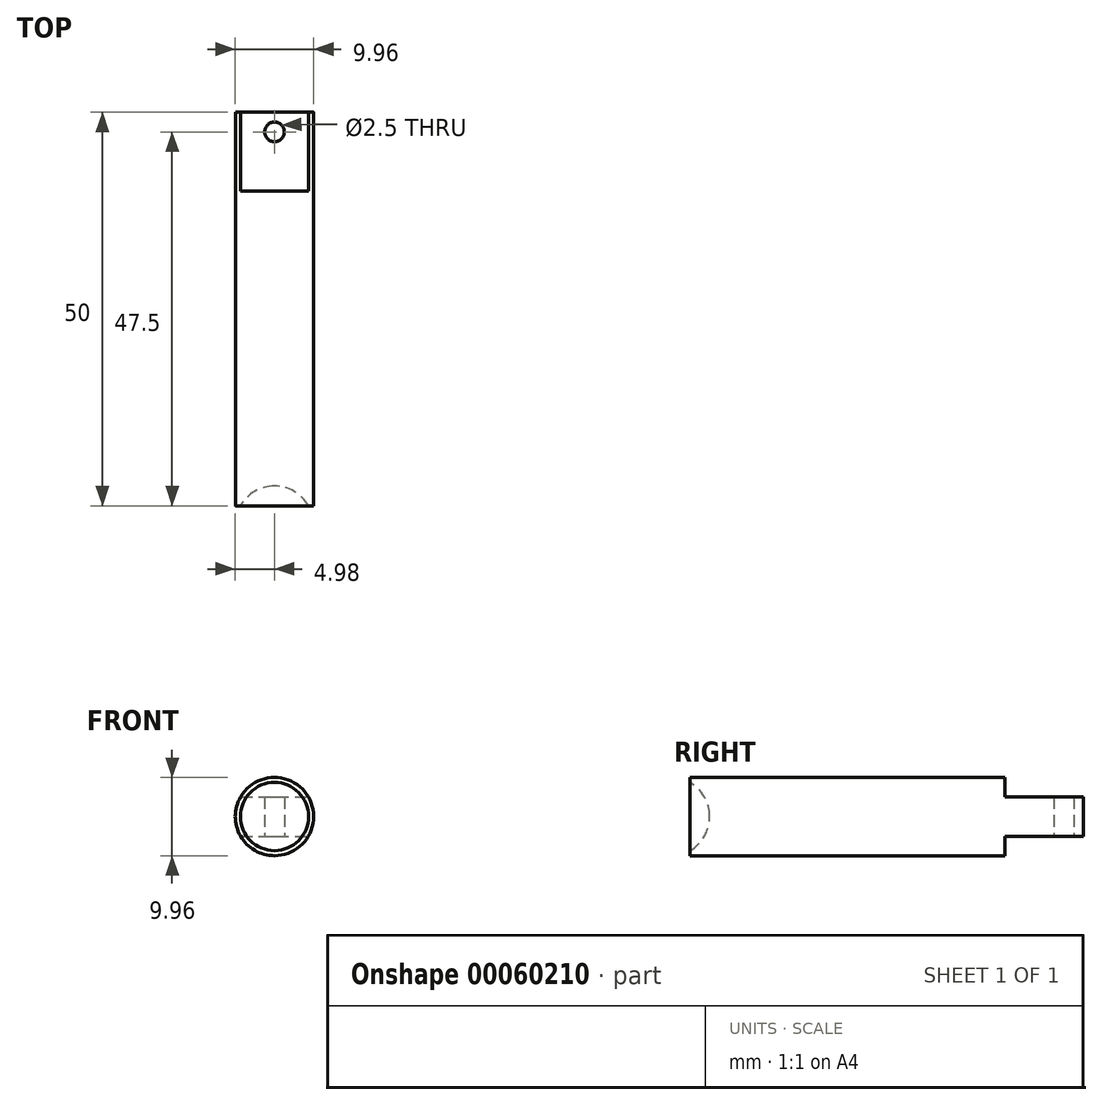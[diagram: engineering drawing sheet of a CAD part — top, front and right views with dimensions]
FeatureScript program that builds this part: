
annotation { "Feature Type Name" : "Feature", "Feature Type Description" : "" }
export const myFeature = defineFeature(function(context is Context, id is Id, definition is map)
    precondition{}
    {
        {
            var Q0;
            Q0=qCreatedBy(makeId("Front.planeOp"),FACE);
            var sketch = newSketch(context, id + "F0", { "sketchPlane" : qUnion([Q0])});
            skCircle(sketch, "E0", {"center": v(0, 0) * mm, "radius": 4.98 * mm});
            skSolve(sketch);
        }
        {
            var Q0;
            Q0 = qSketchRegion(id + "F0", true);
            extrude(context, id + "F1", {"entities" : qUnion([Q0]), "depth" : 50 * mm});
        }
        {
            var Q0;
            Q0=qCreatedBy(makeId("Right.planeOp"),FACE);
            var sketch = newSketch(context, id + "F2", { "sketchPlane" : qUnion([Q0])});
            skArc(sketch, "E1", {"start": v(-47.5, 0) * mm, "mid": v(-48.17, 2.5) * mm, "end": v(-50, 4.33) * mm});
            skLineSegment(sketch, "E2", {"start": v(-50, 4.33) * mm, "end": v(-52.5, 0) * mm});
            skLineSegment(sketch, "E3", {"start": v(-52.5, 0) * mm, "end": v(-47.5, 0) * mm});
            skPoint(sketch, "E4.orphan", {"position": v(-50, -4.33) * mm});
            skSolve(sketch);
        }
        {
            var Q0;
            Q0 = qSketchRegion(id + "F2", true);
            var Q1;
            Q1=sQuery(id+"F2.wireOp",EDGE,"E3");
            revolve(context, id + "F3", {"operationType" : NewBodyOperationType.REMOVE, "entities" : qUnion([Q0]), "axis" : qUnion([Q1]), "revolveType" : RevolveType.FULL, "oppositeDirection" : true});
        }
        {
            var Q0;
            Q0=qCreatedBy(makeId("Right.planeOp"),FACE);
            var sketch = newSketch(context, id + "F4", { "sketchPlane" : qUnion([Q0])});
            skLineSegment(sketch, "E5.bottom", {"start": v(-10, 33.44) * mm, "end": v(26.94, 33.44) * mm});
            skLineSegment(sketch, "E5.top", {"start": v(-10, 2.5) * mm, "end": v(26.94, 2.5) * mm});
            skLineSegment(sketch, "E5.left", {"start": v(-10, 33.44) * mm, "end": v(-10, 2.5) * mm});
            skLineSegment(sketch, "E5.right", {"start": v(26.94, 33.44) * mm, "end": v(26.94, 2.5) * mm});
            skLineSegment(sketch, "E6.bottom", {"start": v(-10, -2.5) * mm, "end": v(26.96, -2.5) * mm});
            skLineSegment(sketch, "E6.top", {"start": v(-10, -54.36) * mm, "end": v(26.96, -54.36) * mm});
            skLineSegment(sketch, "E6.left", {"start": v(-10, -2.5) * mm, "end": v(-10, -54.36) * mm});
            skLineSegment(sketch, "E6.right", {"start": v(26.96, -2.5) * mm, "end": v(26.96, -54.36) * mm});
            skSolve(sketch);
        }
        {
            var Q0;
            Q0 = qSketchRegion(id + "F4", true);
            extrude(context, id + "F5", {"entities" : qUnion([Q0]), "operationType" : NewBodyOperationType.REMOVE, "endBound" : BoundingType.THROUGH_ALL, "oppositeDirection" : true, "depth" : 25 * mm, "hasSecondDirection" : true, "secondDirectionBound" : SecondDirectionBoundingType.THROUGH_ALL, "secondDirectionOppositeDirection" : false, "secondDirectionDepth" : 25 * mm});
        }
        {
            var Q0;
            Q0=makeQuery(id+"F5.boolean.opBoolean","COPY",FACE,{"derivedFrom":makeQuery(id+"F5.opExtrude","SWEPT_FACE",FACE,{"disambiguationData":[OSD([sQuery(id+"F4.wireOp",EDGE,"E6.bottom")])]})});
            var sketch = newSketch(context, id + "F6", { "sketchPlane" : qUnion([Q0])});
            skCircle(sketch, "E7", {"center": v(0, 2.5) * mm, "radius": 1.25 * mm});
            skSolve(sketch);
        }
        {
            var Q0;
            Q0 = qSketchRegion(id + "F6", true);
            extrude(context, id + "F7", {"entities" : qUnion([Q0]), "operationType" : NewBodyOperationType.REMOVE, "oppositeDirection" : true, "depth" : 25 * mm});
        }
    });
